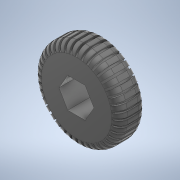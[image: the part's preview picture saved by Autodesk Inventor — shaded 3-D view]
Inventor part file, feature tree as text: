
AUTODESK INVENTOR PART (.ipt)
format: ipt  version: 2020.4 (Build 244396000, 396)  size: 667,648 bytes
history: native  units: mm
features: extrude x2, sketch x2, fillet x1, pattern_circular x1
ambient origin geometry x8: Origin, YZ Plane, XZ Plane, XY Plane, X Axis, Y Axis, Z Axis, Center Point
bodies: Solid1 (feature_tree)
feature tree (6):
  extrude  "Extrusion1"  Depth=16.0mm
  fillet  "Fillet1"  Radius=5.0mm
  extrude  "Extrusion2"  Depth=0.4mm
  pattern_circular  "Circular Pattern1"  [2 undecoded]
  sketch  "Sketch1"  dims[d1=5.6mm d2=16.0mm d3=5.0mm d4=0.0mm]
  sketch  "Sketch2"  dims[d5=90.0deg d6=6.5mm d7=3.25mm d8=0.4mm d9=0.0mm d10=400.0mm d11=360.0deg d13=1.5mm]
note: 2 required parameter values undecoded (feature->parameter linkage not recoverable at this tier; creation-order binding heuristic only, values carry confidence <= 0.55)
